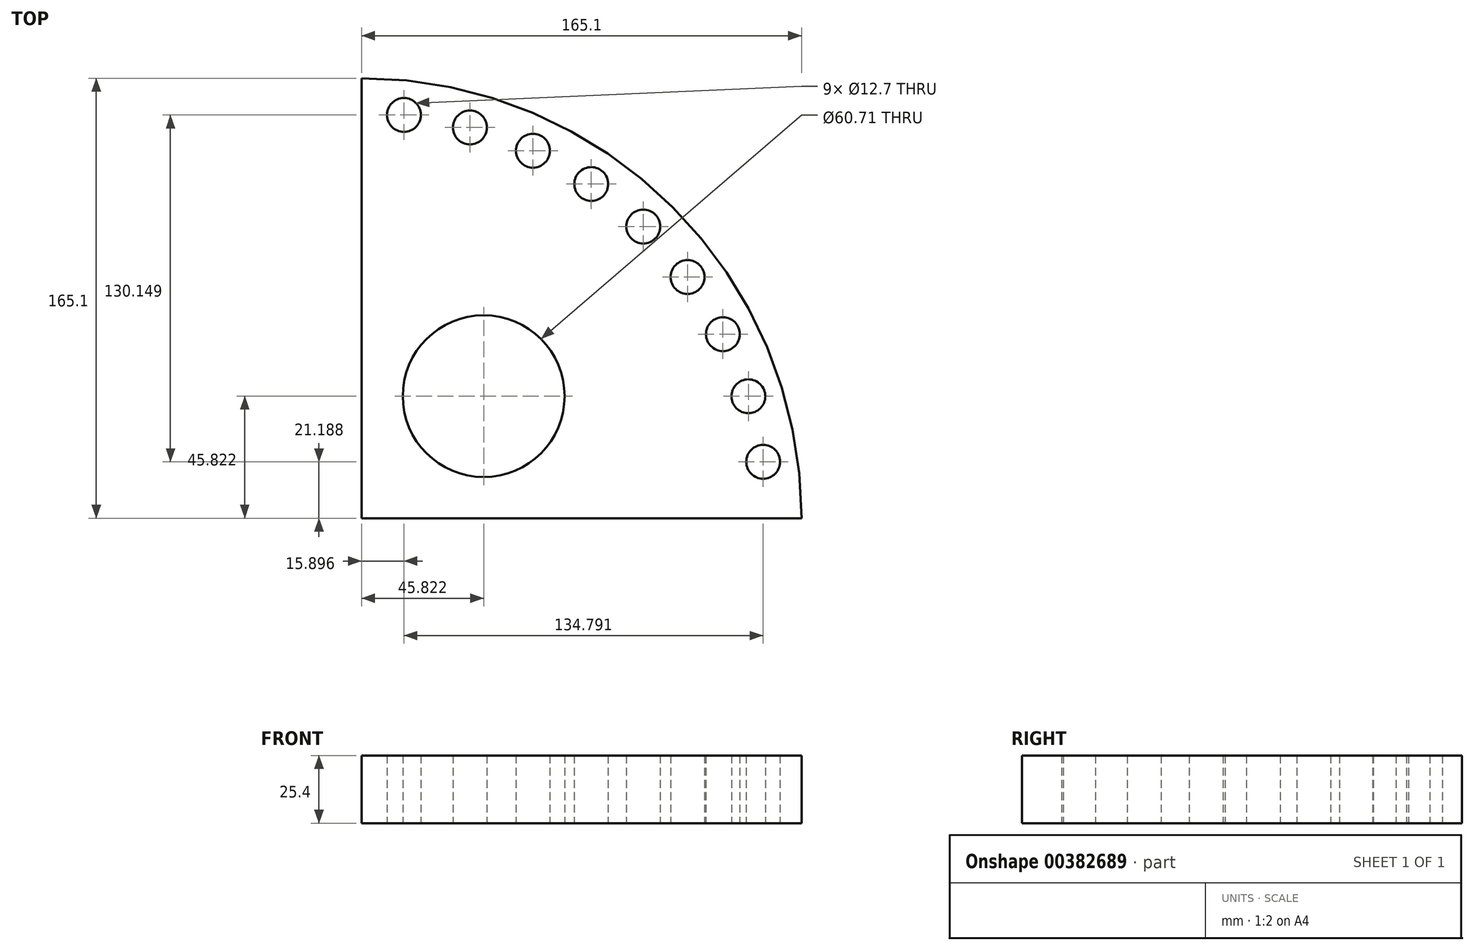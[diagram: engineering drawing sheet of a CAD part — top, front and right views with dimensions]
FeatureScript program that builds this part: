
annotation { "Feature Type Name" : "Feature", "Feature Type Description" : "" }
export const myFeature = defineFeature(function(context is Context, id is Id, definition is map)
    precondition{}
    {
        {
            var Q0;
            Q0=qCreatedBy(makeId("Top.planeOp"),FACE);
            var sketch = newSketch(context, id + "F0", { "sketchPlane" : qUnion([Q0])});
            skCircle(sketch, "E0", {"center": v(-152.4, 0) * mm, "radius": 165.1 * mm});
            skLineSegment(sketch, "E1", {"start": v(-152.4, 0) * mm, "end": v(-152.4, 165.1) * mm});
            skLineSegment(sketch, "E2", {"start": v(-152.4, 0) * mm, "end": v(12.7, 0) * mm});
            skCircle(sketch, "E3", {"center": v(-106.58, 45.82) * mm, "radius": 30.35 * mm});
            skCircle(sketch, "E4", {"center": v(-136.5, 151.34) * mm, "radius": 6.35 * mm});
            skCircle(sketch, "E5.1.0", {"center": v(-111.74, 146.64) * mm, "radius": 6.35 * mm});
            skCircle(sketch, "E5.2.0", {"center": v(-88.1, 137.92) * mm, "radius": 6.35 * mm});
            skCircle(sketch, "E5.3.0", {"center": v(-66.22, 125.41) * mm, "radius": 6.35 * mm});
            skCircle(sketch, "E5.4.0", {"center": v(-46.7, 109.47) * mm, "radius": 6.35 * mm});
            skCircle(sketch, "E5.5.0", {"center": v(-30.08, 90.52) * mm, "radius": 6.35 * mm});
            skCircle(sketch, "E5.6.0", {"center": v(-16.82, 69.1) * mm, "radius": 6.35 * mm});
            skCircle(sketch, "E5.7.0", {"center": v(-7.28, 45.77) * mm, "radius": 6.35 * mm});
            skCircle(sketch, "E5.8.0", {"center": v(-1.71, 21.19) * mm, "radius": 6.35 * mm});
            skLineSegment(sketch, "E5.anchor1", {"start": v(-152.4, 0) * mm, "end": v(-136.5, 151.34) * mm, "construction": true});
            skLineSegment(sketch, "E5.anchor2", {"start": v(-152.4, 0) * mm, "end": v(-1.71, 21.19) * mm, "construction": true});
            skSolve(sketch);
        }
        {
            var Q0;
            {var subQ0=sQuery(id+"F0.wireOp",EDGE,"E1");Q0=makeQuery(id+"F0.imprint","IMPRINT",FACE,{"disambiguationData":[TD([[makeQuery(id+"F0.imprint","IMPRINT",EDGE,{"derivedFrom":subQ0}),-1.0]])]});}
            extrude(context, id + "F1", {"entities" : qUnion([Q0]), "depth" : 25.4 * mm});
        }
    });
